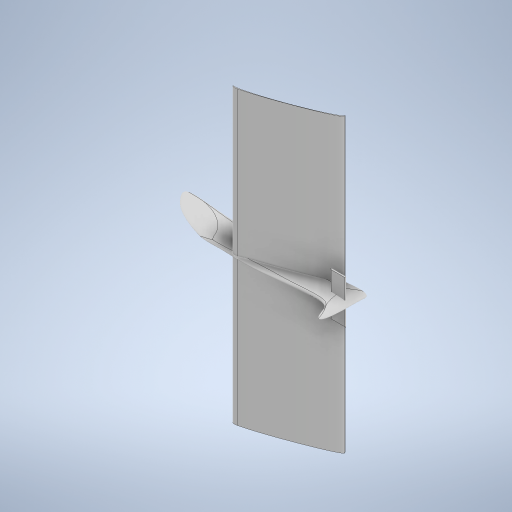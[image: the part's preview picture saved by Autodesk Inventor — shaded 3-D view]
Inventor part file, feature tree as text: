
AUTODESK INVENTOR PART (.ipt)
format: ipt  version: 2024 (Build 280153000, 153)  size: 697,856 bytes
history: native  units: mm
features: other x3, extrude x2, fillet x1
ambient origin geometry x8: Origin, YZ Plane, XZ Plane, XY Plane, X Axis, Y Axis, Z Axis, Center Point
bodies: Body1 (feature_tree), Body2 (feature_tree)
feature tree (6):
  other  "ソリッド1"
  extrude  "押し出し1"  Depth=1.047198mm TaperAngle=0.0deg
  extrude  "押し出し2"  Depth=150.0mm TaperAngle=0.0deg
  other  "フォーム2"
  fillet  "フィレット11"  Radius=3.490659mm
  other  "ソリッド2"
